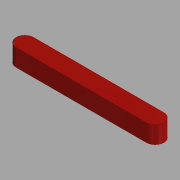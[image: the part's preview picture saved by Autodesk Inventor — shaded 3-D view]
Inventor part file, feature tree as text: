
AUTODESK INVENTOR PART (.ipt)
format: ipt  version: 2014 SP2 (Build 180246200, 246)  size: 127,488 bytes
history: native  units: mm
features: other x2, extrude x1
ambient origin geometry x8: Origin, YZ Plane, XZ Plane, XY Plane, X Axis, Y Axis, Z Axis, Center Point
bodies: Body1 (feature_tree)
feature tree (3):
  other  "Těleso1"
  extrude  "Vysunutí1"  Depth=2.0mm TaperAngle=0.0deg
  other  "Referenční1"
